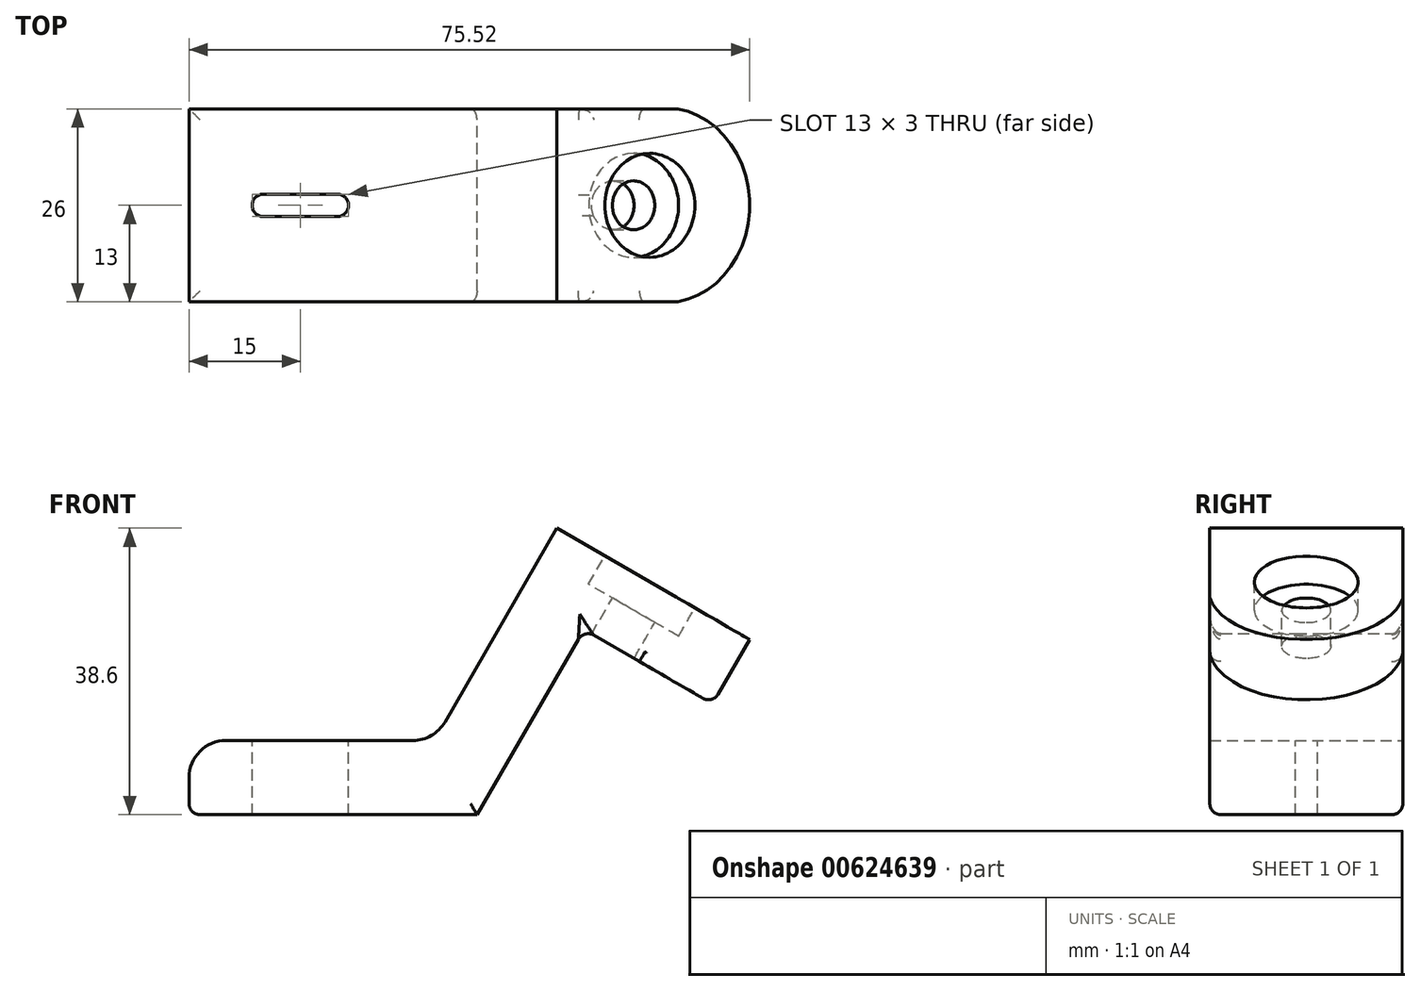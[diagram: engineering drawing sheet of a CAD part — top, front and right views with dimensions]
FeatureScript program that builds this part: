
annotation { "Feature Type Name" : "Feature", "Feature Type Description" : "" }
export const myFeature = defineFeature(function(context is Context, id is Id, definition is map)
    precondition{}
    {
        {
            var Q0;
            Q0=qCreatedBy(makeId("Front.planeOp"),FACE);
            var sketch = newSketch(context, id + "F0", { "sketchPlane" : qUnion([Q0])});
            skLineSegment(sketch, "E0", {"start": v(0, 0) * mm, "end": v(38.8, 0) * mm});
            skLineSegment(sketch, "E1", {"start": v(38.8, 0) * mm, "end": v(58.2, 33.6) * mm});
            skLineSegment(sketch, "E2", {"start": v(58.2, 33.6) * mm, "end": v(49.54, 38.6) * mm});
            skLineSegment(sketch, "E3", {"start": v(0, 0) * mm, "end": v(0, 4.91) * mm});
            skLineSegment(sketch, "E4", {"start": v(5, 10) * mm, "end": v(30.14, 10) * mm});
            skLineSegment(sketch, "E5", {"start": v(49.54, 38.6) * mm, "end": v(34.47, 12.5) * mm});
            skPoint(sketch, "E6", {"position": v(33.03, 10) * mm});
            skArc(sketch, "E7.filletArc", {"start": v(30.14, 10) * mm, "mid": v(32.64, 10.67) * mm, "end": v(34.47, 12.5) * mm});
            skPoint(sketch, "E8.visualSharp", {"position": v(0, 10) * mm});
            skLineSegment(sketch, "E9", {"start": v(5, 10) * mm, "end": v(5, 10) * mm});
            skLineSegment(sketch, "E10", {"start": v(0, 4.91) * mm, "end": v(0, 5) * mm});
            skArc(sketch, "E11.filletArc", {"start": v(5, 10) * mm, "mid": v(1.46, 8.54) * mm, "end": v(0, 5) * mm});
            skLineSegment(sketch, "E12", {"start": v(58.2, 33.6) * mm, "end": v(75.52, 23.6) * mm});
            skLineSegment(sketch, "E13", {"start": v(75.52, 23.6) * mm, "end": v(70.52, 14.94) * mm});
            skLineSegment(sketch, "E14", {"start": v(70.52, 14.94) * mm, "end": v(53.2, 24.94) * mm});
            skSolve(sketch);
        }
        {
            var Q0;
            {var subQ0=sQuery(id+"F0.wireOp",EDGE,"E12");Q0=makeQuery(id+"F0.imprint","IMPRINT",FACE,{"disambiguationData":[TD([[makeQuery(id+"F0.imprint","IMPRINT",EDGE,{"derivedFrom":subQ0}),-1.0]])]});}
            var Q1;
            {var subQ3=sQuery(id+"F0.wireOp",EDGE,"E0");Q1=makeQuery(id+"F0.imprint","IMPRINT",FACE,{"disambiguationData":[TD([[makeQuery(id+"F0.imprint","IMPRINT",EDGE,{"derivedFrom":subQ3}),1.0]])]});}
            extrude(context, id + "F1", {"entities" : qUnion([Q0, Q1]), "depth" : 26 * mm, "offsetDistance" : 25 * mm});
        }
        {
            var Q0;
            Q0=makeQuery(id+"F1.opExtrude","SWEPT_FACE",FACE,{"disambiguationData":[OSD([sQuery(id+"F0.wireOp",EDGE,"E4")])]});
            var sketch = newSketch(context, id + "F2", { "sketchPlane" : qUnion([Q0])});
            skArc(sketch, "E15", {"start": v(10, -11.5) * mm, "mid": v(8.5, -13) * mm, "end": v(10, -14.5) * mm});
            skPoint(sketch, "E15.centerSnap0", {"position": v(5, -13) * mm});
            skArc(sketch, "E16", {"start": v(20, -14.5) * mm, "mid": v(21.5, -13) * mm, "end": v(20, -11.5) * mm});
            skLineSegment(sketch, "E17", {"start": v(20, -14.5) * mm, "end": v(10, -14.5) * mm});
            skLineSegment(sketch, "E18", {"start": v(20, -11.5) * mm, "end": v(10, -11.5) * mm});
            skSolve(sketch);
        }
        {
            var Q0;
            Q0 = qSketchRegion(id + "F2", true);
            var Q1;
            Q1=makeQuery(id+"F2.imprint","IMPRINT",FACE,{"disambiguationData":[TD([[makeQuery(id+"F2.imprint","IMPRINT",EDGE,{"derivedFrom":sQuery(id+"F2.wireOp",EDGE,"E15")}),1.0]])]});
            extrude(context, id + "F3", {"entities" : qUnion([Q0, Q1]), "operationType" : NewBodyOperationType.REMOVE, "oppositeDirection" : true, "depth" : 25 * mm, "offsetDistance" : 25 * mm});
        }
        {
            var Q0;
            Q0=makeQuery(id+"F1.opExtrude","SWEPT_FACE",FACE,{"disambiguationData":[OSD([sQuery(id+"F0.wireOp",EDGE,"E2"),sQuery(id+"F0.wireOp",EDGE,"E12")])]});
            var sketch = newSketch(context, id + "F4", { "sketchPlane" : qUnion([Q0])});
            skPoint(sketch, "E19.centerSnap0", {"position": v(53.6, -13) * mm});
            skArc(sketch, "E20", {"start": v(38.6, -26) * mm, "mid": v(53.6, -13) * mm, "end": v(38.6, 0) * mm});
            skLineSegment(sketch, "E21", {"start": v(38.6, -26) * mm, "end": v(53.6, -26) * mm});
            skLineSegment(sketch, "E22", {"start": v(53.6, -26) * mm, "end": v(53.6, 0) * mm});
            skLineSegment(sketch, "E23", {"start": v(53.6, 0) * mm, "end": v(38.6, 0) * mm});
            skSolve(sketch);
        }
        {
            var Q0;
            {var subQ0=sQuery(id+"F4.wireOp",EDGE,"E21");var subQ1=sQuery(id+"F4.wireOp",EDGE,"E20");var subQ3=makeQuery(id+"F4.imprint","INTERSECT",VERTEX,{"derivedFrom":[subQ1,subQ0]});Q0=makeQuery(id+"F4.imprint","IMPRINT",FACE,{"disambiguationData":[TD([[makeQuery(id+"F4.imprint","IMPRINT",EDGE,{"disambiguationData":[TD([[subQ3,1.0]])],"derivedFrom":subQ1}),1.0]])]});}
            var Q1;
            {var subQ0=sQuery(id+"F4.wireOp",EDGE,"E22");var subQ1=sQuery(id+"F4.wireOp",EDGE,"E20");var subQ2=makeQuery(id+"F4.imprint","INTERSECT",VERTEX,{"derivedFrom":[subQ1,subQ0]});Q1=makeQuery(id+"F4.imprint","IMPRINT",FACE,{"disambiguationData":[TD([[makeQuery(id+"F4.imprint","IMPRINT",EDGE,{"disambiguationData":[TD([[subQ2,-1.0]])],"derivedFrom":subQ1}),-1.0]])]});}
            var Q2;
            {var subQ0=sQuery(id+"F4.wireOp",EDGE,"E23");var subQ1=sQuery(id+"F4.wireOp",EDGE,"E20");var subQ3=makeQuery(id+"F4.imprint","INTERSECT",VERTEX,{"derivedFrom":[subQ1,subQ0]});Q2=makeQuery(id+"F4.imprint","IMPRINT",FACE,{"disambiguationData":[TD([[makeQuery(id+"F4.imprint","IMPRINT",EDGE,{"disambiguationData":[TD([[subQ3,-1.0]])],"derivedFrom":subQ1}),1.0]])]});}
            var Q3;
            {var subQ0=sQuery(id+"F4.wireOp",EDGE,"E21");var subQ1=sQuery(id+"F4.wireOp",EDGE,"E20");var subQ2=makeQuery(id+"F4.imprint","INTERSECT",VERTEX,{"derivedFrom":[subQ1,subQ0]});Q3=makeQuery(id+"F4.imprint","IMPRINT",FACE,{"disambiguationData":[TD([[makeQuery(id+"F4.imprint","IMPRINT",EDGE,{"disambiguationData":[TD([[subQ2,-1.0]])],"derivedFrom":subQ1}),-1.0]])]});}
            extrude(context, id + "F5", {"entities" : qUnion([Q0, Q1, Q2, Q3]), "operationType" : NewBodyOperationType.REMOVE, "oppositeDirection" : true, "depth" : 25 * mm, "offsetDistance" : 25 * mm});
        }
        {
            var Q0;
            Q0=makeQuery(id+"F1.opExtrude","SWEPT_FACE",FACE,{"disambiguationData":[OSD([sQuery(id+"F0.wireOp",EDGE,"E2"),sQuery(id+"F0.wireOp",EDGE,"E12")])]});
            var sketch = newSketch(context, id + "F6", { "sketchPlane" : qUnion([Q0])});
            skCircle(sketch, "E24", {"center": v(38.09, -13) * mm, "radius": 7 * mm});
            skPoint(sketch, "E24.centerSnap0", {"position": v(53.6, -13) * mm});
            skSolve(sketch);
        }
        {
            var Q0;
            Q0=makeQuery(id+"F6.imprint","IMPRINT",FACE,{"disambiguationData":[TD([[makeQuery(id+"F6.imprint","IMPRINT",EDGE,{"derivedFrom":sQuery(id+"F6.wireOp",EDGE,"E24")}),1.0]])]});
            extrude(context, id + "F7", {"entities" : qUnion([Q0]), "operationType" : NewBodyOperationType.REMOVE, "oppositeDirection" : true, "depth" : 4.4 * mm, "offsetDistance" : 25 * mm});
        }
        {
            var Q0;
            Q0=makeQuery(id+"F7.boolean.opBoolean","COPY",FACE,{"derivedFrom":makeQuery(id+"F7.opExtrude","CAP_FACE",FACE,{"disambiguationData":[OSD([sQuery(id+"F6.wireOp",EDGE,"E24")])],"isStart":false})});
            var sketch = newSketch(context, id + "F8", { "sketchPlane" : qUnion([Q0])});
            skCircle(sketch, "E25", {"center": v(38.09, -13) * mm, "radius": 3.3 * mm});
            skSolve(sketch);
        }
        {
            var Q0;
            Q0=makeQuery(id+"F8.imprint","IMPRINT",FACE,{"disambiguationData":[TD([[makeQuery(id+"F8.imprint","IMPRINT",EDGE,{"derivedFrom":sQuery(id+"F8.wireOp",EDGE,"E25")}),1.0]])]});
            extrude(context, id + "F9", {"entities" : qUnion([Q0]), "operationType" : NewBodyOperationType.REMOVE, "oppositeDirection" : true, "depth" : 25 * mm, "offsetDistance" : 25 * mm});
        }
        {
            var Q0;
            Q0=makeQuery(id+"F1.opExtrude","CAP_EDGE",EDGE,{"disambiguationData":[OSD([sQuery(id+"F0.wireOp",EDGE,"E0")])],"isStart":false});
            var Q1;
            Q1=makeQuery(id+"F1.opExtrude","CAP_EDGE",EDGE,{"disambiguationData":[OSD([sQuery(id+"F0.wireOp",EDGE,"E1")])],"isStart":false});
            var Q2;
            Q2=makeQuery(id+"F1.opExtrude","CAP_EDGE",EDGE,{"disambiguationData":[OSD([sQuery(id+"F0.wireOp",EDGE,"E14")])],"isStart":false});
            var Q3;
            Q3=makeQuery(id+"F1.opExtrude","CAP_EDGE",EDGE,{"disambiguationData":[OSD([sQuery(id+"F0.wireOp",EDGE,"E14")])],"isStart":true});
            var Q4;
            Q4=makeQuery(id+"F1.opExtrude","CAP_EDGE",EDGE,{"disambiguationData":[OSD([sQuery(id+"F0.wireOp",EDGE,"E1")])],"isStart":true});
            var Q5;
            Q5=makeQuery(id+"F1.opExtrude","CAP_EDGE",EDGE,{"disambiguationData":[OSD([sQuery(id+"F0.wireOp",EDGE,"E0")])],"isStart":true});
            var Q6;
            Q6=makeQuery(id+"F1.opExtrude","SWEPT_EDGE",EDGE,{"disambiguationData":[OSD([sQuery(id+"F0.wireOp",EDGE,"E0"),sQuery(id+"F0.wireOp",EDGE,"E3")])]});
            fillet(context, id + "F10", {"entities" : qUnion([Q0, Q1, Q2, Q3, Q4, Q5, Q6]), "radius" : 1.5 * mm, "tangentPropagation" : true, "allowEdgeOverflow" : false});
        }
        {
            var Q0;
            {var subQ0=sQuery(id+"F4.wireOp",EDGE,"E20");var subQ1=makeQuery(id+"F4.imprint","INTERSECT",VERTEX,{"derivedFrom":[subQ0,sQuery(id+"F4.wireOp",EDGE,"E22")]});Q0=makeQuery(id+"F5.boolean.opBoolean","INTERSECT",EDGE,{"derivedFrom":[makeQuery(id+"F1.opExtrude","SWEPT_FACE",FACE,{"disambiguationData":[OSD([sQuery(id+"F0.wireOp",EDGE,"E14")])]}),makeQuery(id+"F5.opExtrude","SWEPT_FACE",FACE,{"disambiguationData":[OSD([subQ0]),TDD([makeQuery(id+"F4.imprint","IMPRINT",EDGE,{"disambiguationData":[TD([[makeQuery(id+"F4.imprint","INTERSECT",VERTEX,{"derivedFrom":[subQ0,sQuery(id+"F4.wireOp",EDGE,"E21")]}),-1.0]])],"derivedFrom":subQ0})])]}),makeQuery(id+"F5.opExtrude","SWEPT_FACE",FACE,{"disambiguationData":[OSD([subQ0]),TDD([makeQuery(id+"F4.imprint","IMPRINT",EDGE,{"disambiguationData":[TD([[subQ1,-1.0]])],"derivedFrom":subQ0})])]})]});}
            var Q1;
            Q1=makeQuery(id+"F1.opExtrude","SWEPT_EDGE",EDGE,{"disambiguationData":[OSD([sQuery(id+"F0.wireOp",EDGE,"E1"),sQuery(id+"F0.wireOp",EDGE,"E14")])]});
            fillet(context, id + "F11", {"entities" : qUnion([Q0, Q1]), "radius" : 1.5 * mm, "tangentPropagation" : true, "allowEdgeOverflow" : false});
        }
    });
